# Revit family: NLRS_63_LF_UN_noodverlichting trendlux plafond opbouw_hertek
name_source: partatom
category: Lighting Fixtures
units: mm (PartAtom-declared; Revit-internal decimal feet)

## family parameters
Always vertical = Yes
Cut with Voids When Loaded = No
Light Source = No
OmniClass Number = 23.85.30.21
OmniClass Title = Environmental Detection/Registration
Part Type = Normal
Room Calculation Point = No
Round Connector Dimension = Use Radius
Shared = No
Work Plane-Based = No

## types (2) — shared parameters
Apparent Load = 6 VA
Lamp = LED
Manufacturer = Hertek
NLRS_C_breedte = 90 mm  [stored 0.295276 ft]
NLRS_C_code_fabrikant_gln = 8714253082646
NLRS_C_hoogte = 170 mm  [stored 0.557743 ft]
NLRS_C_lengte = 370 mm  [stored 1.21391 ft]
NLRS_C_materiaal = Polycarbonaat wit
NLRS_C_materiaal_01 = Glass
NLRS_C_materiaal_kleur = wit
NLRS_C_revit_versie = 2020
NLRS_E_c01_radius = 8 mm  [stored 0.0262467 ft]
NLRS_E_c01_schijnbaar_vermogen = 6 VA
NLRS_E_c01_schijnbaar_vermogen_fase_1 = 0 VA
NLRS_E_c01_schijnbaar_vermogen_fase_2 = 0 VA
NLRS_E_c01_schijnbaar_vermogen_fase_3 = 0 VA
NLRS_E_spanning = 230 V
NLRS_E_stroom = 0.0 A
NLRS_S_gewicht_netto = 0.00 kg
URL = www.hertek.eu
Wattage Comments = 2-6W (dimbaar)
batterij = LiFePo4
centraal = No
decentraal = Yes
picto = No
plafondmontage = Yes
vermogensclassificatie = NV
wireless = No
zero-valued in all types: Default Elevation

## per-type parameters (varying)
| type | NLRS_C_code_artikel | NLRS_C_model | NLRS_C_omschrijving | zichtbaar_01 |
| Trendlux Series 3 dec AT opbouw - vluchtwegaanduiding_htk_NTD230-4 | NTD230-4 | Trendlux Series 3 dec AT opbouw top LiFePo4 10/8YW | Trendlux Series 3 dec AT opbouw top LiFePo4 10/8YW | Yes |
| Trendlux Series 3 dec AT opbouw - vluchtwegverlichting_htk_NTD210-4 | NTD210-4 | Trendlux Series 3 dec AT opbouw LiFePo4 10/8YW | Trendlux Series 3 dec AT opbouw LiFePo4 10/8YW | No |

note: [stored X ft] marks values corroborated as IEEE doubles in the binary element streams (Revit-internal decimal feet)

## geometry (parser evidence)
native form markers: Blend x8, Sweep x37
no freeform markers — native parametric forms only
